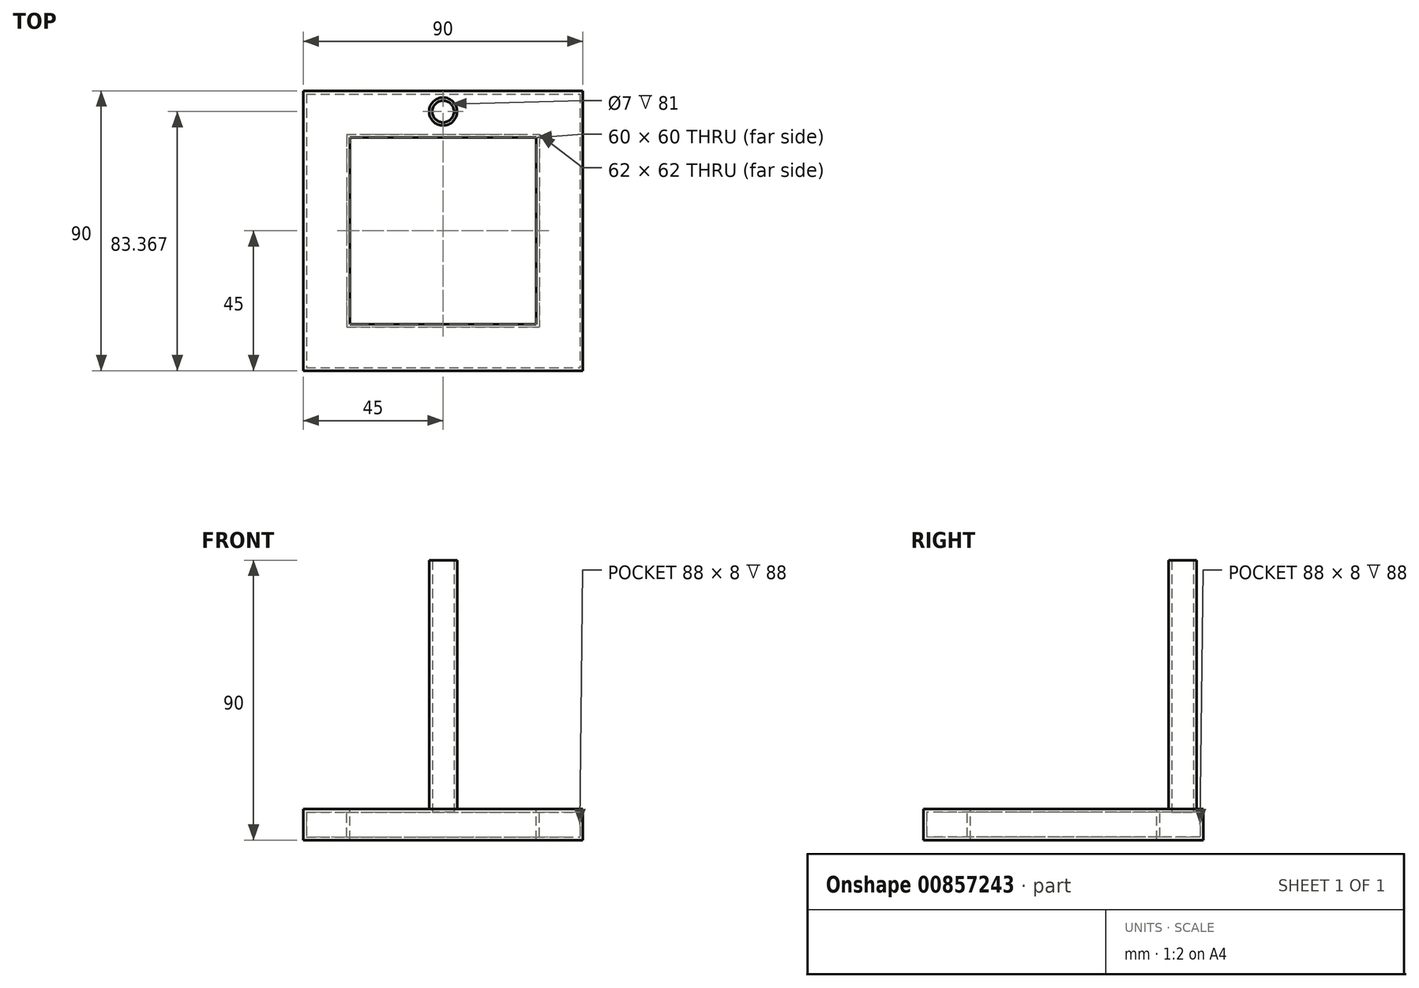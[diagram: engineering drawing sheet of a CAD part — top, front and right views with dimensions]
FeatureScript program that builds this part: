
annotation { "Feature Type Name" : "Feature", "Feature Type Description" : "" }
export const myFeature = defineFeature(function(context is Context, id is Id, definition is map)
    precondition{}
    {
        {
            var Q0;
            Q0=qCreatedBy(makeId("Top.planeOp"),FACE);
            var sketch = newSketch(context, id + "F0", { "sketchPlane" : qUnion([Q0])});
            skLineSegment(sketch, "E0.bottom", {"start": v(-45, 45) * mm, "end": v(45, 45) * mm});
            skLineSegment(sketch, "E0.top", {"start": v(-45, -45) * mm, "end": v(45, -45) * mm});
            skLineSegment(sketch, "E0.left", {"start": v(-45, 45) * mm, "end": v(-45, -45) * mm});
            skLineSegment(sketch, "E0.right", {"start": v(45, 45) * mm, "end": v(45, -45) * mm});
            skPoint(sketch, "E0.middle", {"position": v(0, 0) * mm});
            skSolve(sketch);
        }
        {
            var Q0;
            Q0 = qSketchRegion(id + "F0", true);
            extrude(context, id + "F1", {"entities" : qUnion([Q0]), "depth" : 10 * mm, "offsetDistance" : 25 * mm});
        }
        {
            var Q0;
            Q0=makeQuery(id+"F1.opExtrude","CAP_FACE",FACE,{"disambiguationData":[OSD([sQuery(id+"F0.wireOp",EDGE,"E0.bottom"),sQuery(id+"F0.wireOp",EDGE,"E0.top"),sQuery(id+"F0.wireOp",EDGE,"E0.left"),sQuery(id+"F0.wireOp",EDGE,"E0.right")])],"isStart":false});
            var sketch = newSketch(context, id + "F2", { "sketchPlane" : qUnion([Q0])});
            skLineSegment(sketch, "E1.bottom", {"start": v(-30, 30) * mm, "end": v(30, 30) * mm});
            skLineSegment(sketch, "E1.top", {"start": v(-30, -30) * mm, "end": v(30, -30) * mm});
            skLineSegment(sketch, "E1.left", {"start": v(-30, 30) * mm, "end": v(-30, -30) * mm});
            skLineSegment(sketch, "E1.right", {"start": v(30, 30) * mm, "end": v(30, -30) * mm});
            skPoint(sketch, "E1.middle", {"position": v(0, 0) * mm});
            skSolve(sketch);
        }
        {
            var Q0;
            Q0 = qSketchRegion(id + "F2", true);
            extrude(context, id + "F3", {"entities" : qUnion([Q0]), "operationType" : NewBodyOperationType.REMOVE, "oppositeDirection" : true, "depth" : 10 * mm, "offsetDistance" : 25 * mm});
        }
        {
            var Q0;
            Q0=makeQuery(id+"F1.opExtrude","CAP_FACE",FACE,{"disambiguationData":[OSD([sQuery(id+"F0.wireOp",EDGE,"E0.bottom"),sQuery(id+"F0.wireOp",EDGE,"E0.top"),sQuery(id+"F0.wireOp",EDGE,"E0.left"),sQuery(id+"F0.wireOp",EDGE,"E0.right")])],"isStart":false});
            var sketch = newSketch(context, id + "F4", { "sketchPlane" : qUnion([Q0])});
            skCircle(sketch, "E2", {"center": v(0, 38.37) * mm, "radius": 4.5 * mm});
            skSolve(sketch);
        }
        {
            var Q0;
            Q0 = qSketchRegion(id + "F4", true);
            extrude(context, id + "F5", {"entities" : qUnion([Q0]), "operationType" : NewBodyOperationType.ADD, "depth" : 80 * mm, "offsetDistance" : 25 * mm});
        }
        {
            var Q0;
            Q0=makeQuery(id+"F5.opExtrude","CAP_FACE",FACE,{"disambiguationData":[OSD([sQuery(id+"F4.wireOp",EDGE,"E2")])],"isStart":false});
            shell(context, id + "F6", {"entities" : qUnion([Q0]), "thickness" : 1 * mm});
        }
    });
